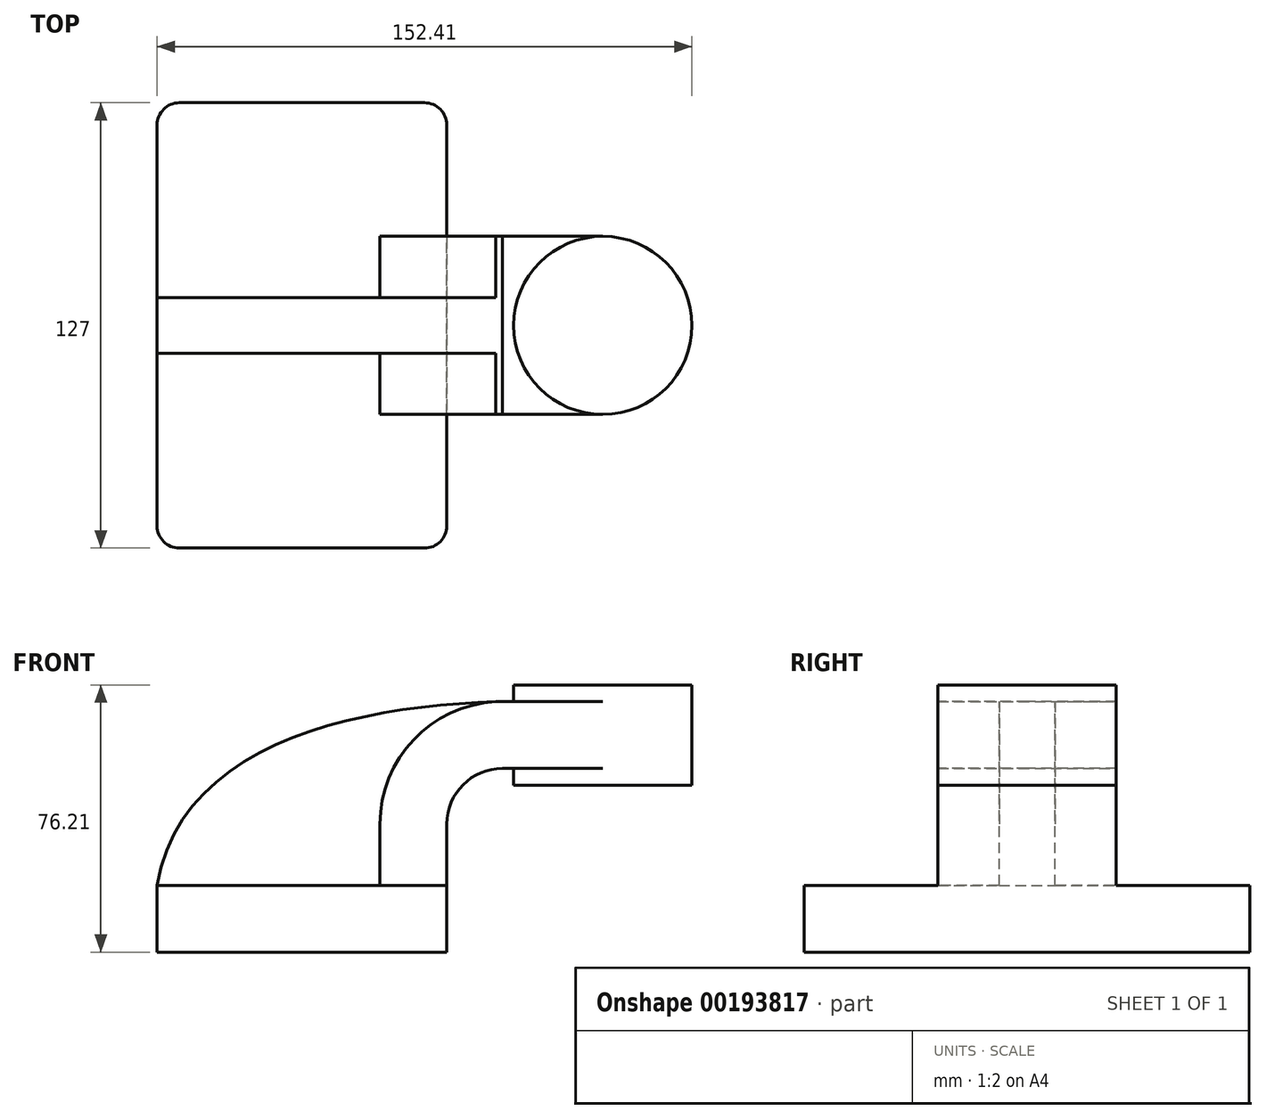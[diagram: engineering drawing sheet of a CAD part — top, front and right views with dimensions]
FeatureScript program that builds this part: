
annotation { "Feature Type Name" : "Feature", "Feature Type Description" : "" }
export const myFeature = defineFeature(function(context is Context, id is Id, definition is map)
    precondition{}
    {
        {
            var Q0;
            Q0=qCreatedBy(makeId("Front.planeOp"),FACE);
            var sketch = newSketch(context, id + "F0", { "sketchPlane" : qUnion([Q0])});
            skLineSegment(sketch, "E0.bottom", {"start": v(41.27, 9.53) * mm, "end": v(-41.28, 9.52) * mm});
            skLineSegment(sketch, "E0.top", {"start": v(41.28, -9.52) * mm, "end": v(-41.27, -9.53) * mm});
            skLineSegment(sketch, "E0.left", {"start": v(41.27, 9.53) * mm, "end": v(41.28, -9.52) * mm});
            skLineSegment(sketch, "E0.right", {"start": v(-41.28, 9.52) * mm, "end": v(-41.27, -9.53) * mm});
            skPoint(sketch, "E0.middle", {"position": v(0, 0) * mm});
            skLineSegment(sketch, "E1", {"start": v(41.27, 9.53) * mm, "end": v(41.27, 26.99) * mm});
            skArc(sketch, "E2", {"start": v(41.27, 26.99) * mm, "mid": v(45.92, 38.21) * mm, "end": v(57.15, 42.86) * mm});
            skLineSegment(sketch, "E3", {"start": v(57.15, 42.86) * mm, "end": v(85.72, 42.86) * mm});
            skLineSegment(sketch, "E4.bottom", {"start": v(111.12, 66.68) * mm, "end": v(60.32, 66.68) * mm});
            skLineSegment(sketch, "E4.top", {"start": v(111.12, 38.1) * mm, "end": v(60.32, 38.1) * mm});
            skLineSegment(sketch, "E4.left", {"start": v(111.12, 66.68) * mm, "end": v(111.12, 38.1) * mm});
            skLineSegment(sketch, "E4.right", {"start": v(60.32, 66.68) * mm, "end": v(60.32, 38.1) * mm});
            skPoint(sketch, "E4.middle", {"position": v(85.72, 52.39) * mm});
            skLineSegment(sketch, "E5.0", {"start": v(57.15, 61.91) * mm, "end": v(85.72, 61.91) * mm});
            skArc(sketch, "E5.1", {"start": v(22.22, 26.99) * mm, "mid": v(32.45, 51.68) * mm, "end": v(57.15, 61.91) * mm});
            skLineSegment(sketch, "E5.2", {"start": v(22.22, 9.53) * mm, "end": v(22.22, 26.99) * mm});
            skLineSegment(sketch, "E6", {"start": v(85.72, 38.1) * mm, "end": v(85.72, 66.68) * mm});
            skFitSpline(sketch, "E7", {"points": [v(-41.28, 9.53) * mm, v(57.15, 61.91) * mm], "startDerivative": vector(20.45, 124.95) * mm, "endDerivative": vector(117.74, 2.76) * mm});
            skSolve(sketch);
        }
        {
            var Q0;
            Q0=makeQuery(id+"F0.imprint","IMPRINT",FACE,{"disambiguationData":[TD([[makeQuery(id+"F0.imprint","IMPRINT",EDGE,{"derivedFrom":sQuery(id+"F0.wireOp",EDGE,"E0.top")}),-1.0]])]});
            extrude(context, id + "F1", {"entities" : qUnion([Q0]), "endBound" : BoundingType.SYMMETRIC, "oppositeDirection" : true, "depth" : 127 * mm});
        }
        {
            var Q0;
            {var subQ9=sQuery(id+"F0.wireOp",EDGE,"E1");Q0=makeQuery(id+"F0.imprint","IMPRINT",FACE,{"disambiguationData":[TD([[makeQuery(id+"F0.imprint","IMPRINT",EDGE,{"derivedFrom":subQ9}),1.0]])]});}
            var Q1;
            {var subQ0=sQuery(id+"F0.wireOp",EDGE,"E6");var subQ1=sQuery(id+"F0.wireOp",EDGE,"E3");var subQ2=makeQuery(id+"F0.imprint","INTERSECT",VERTEX,{"derivedFrom":[subQ1,subQ0]});Q1=makeQuery(id+"F0.imprint","IMPRINT",FACE,{"disambiguationData":[TD([[makeQuery(id+"F0.imprint","IMPRINT",EDGE,{"disambiguationData":[TD([[subQ2,1.0]])],"derivedFrom":subQ1}),1.0]])]});}
            extrude(context, id + "F2", {"entities" : qUnion([Q0, Q1]), "operationType" : NewBodyOperationType.ADD, "endBound" : BoundingType.SYMMETRIC, "depth" : 50.8 * mm});
        }
        {
            var Q0;
            {var subQ3=sQuery(id+"F0.wireOp",EDGE,"E5.2");Q0=makeQuery(id+"F0.imprint","IMPRINT",FACE,{"disambiguationData":[TD([[makeQuery(id+"F0.imprint","IMPRINT",EDGE,{"derivedFrom":subQ3}),1.0]])]});}
            extrude(context, id + "F3", {"entities" : qUnion([Q0]), "operationType" : NewBodyOperationType.ADD, "endBound" : BoundingType.SYMMETRIC, "depth" : 15.88 * mm});
        }
        {
            var Q0;
            {var subQ4=sQuery(id+"F0.wireOp",EDGE,"E4.left");Q0=makeQuery(id+"F0.imprint","IMPRINT",FACE,{"disambiguationData":[TD([[makeQuery(id+"F0.imprint","IMPRINT",EDGE,{"derivedFrom":subQ4}),-1.0]])]});}
            var Q1;
            Q1=sQuery(id+"F0.wireOp",EDGE,"E6");
            revolve(context, id + "F4", {"operationType" : NewBodyOperationType.ADD, "entities" : qUnion([Q0]), "axis" : qUnion([Q1]), "revolveType" : RevolveType.FULL});
        }
        {
            var Q0;
            Q0=makeQuery(id+"F1.opExtrude","CAP_EDGE",EDGE,{"disambiguationData":[OSD([sQuery(id+"F0.wireOp",EDGE,"E0.right")])],"isStart":true});
            var Q1;
            Q1=makeQuery(id+"F1.opExtrude","CAP_EDGE",EDGE,{"disambiguationData":[OSD([sQuery(id+"F0.wireOp",EDGE,"E0.left")])],"isStart":true});
            var Q2;
            Q2=makeQuery(id+"F1.opExtrude","CAP_EDGE",EDGE,{"disambiguationData":[OSD([sQuery(id+"F0.wireOp",EDGE,"E0.left")])],"isStart":false});
            var Q3;
            Q3=makeQuery(id+"F1.opExtrude","CAP_EDGE",EDGE,{"disambiguationData":[OSD([sQuery(id+"F0.wireOp",EDGE,"E0.right")])],"isStart":false});
            fillet(context, id + "F5", {"entities" : qUnion([Q0, Q1, Q2, Q3]), "radius" : 6.35 * mm, "tangentPropagation" : true, "allowEdgeOverflow" : false});
        }
    });
